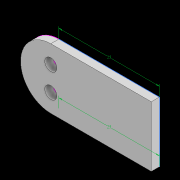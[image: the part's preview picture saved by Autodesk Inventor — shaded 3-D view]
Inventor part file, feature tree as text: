
AUTODESK INVENTOR PART (.ipt)
format: ipt  version: 2022.2 (Build 262287010, 287A)  size: 108,032 bytes
history: native  units: mm
features: sketch x3, extrude x3, hole x1, draft x1, plane x1
ambient origin geometry x8: Origin, YZ Plane, XZ Plane, XY Plane, X Axis, Y Axis, Z Axis, Center Point
bodies: Solid1 (feature_tree)
feature tree (9):
  sketch  "Sketch1"  dims[d0=22.5mm d1=2.5mm]
  extrude  "Extrusion1"  Depth=2.5mm
  extrude  "Extrusion2"  Depth=2.0mm
  hole  "Hole1"  [1 undecoded]
  draft  "FaceDraft1"
  plane  "Work Plane1"
  extrude  "Extrusion3"  Depth=2.0mm
  sketch  "Sketch2"  dims[d2=15.0mm d3=2.0mm]
  sketch  "Sketch3"  dims[d4=2.5mm d5=0.0mm d6=11.0mm d7=0.0mm d8=3.0mm d10=3.0mm d11=6.0mm d12=4.0mm d13=2.0mm d14=90.0deg d15=4.0mm d16=0.0mm d17=20.0mm d18=25.0mm d19=25.0mm d20=2.0mm d21=0.0mm d22=0.436332mm d23=5.5mm]
note: 1 required parameter value undecoded (feature->parameter linkage not recoverable at this tier; creation-order binding heuristic only, values carry confidence <= 0.55)
